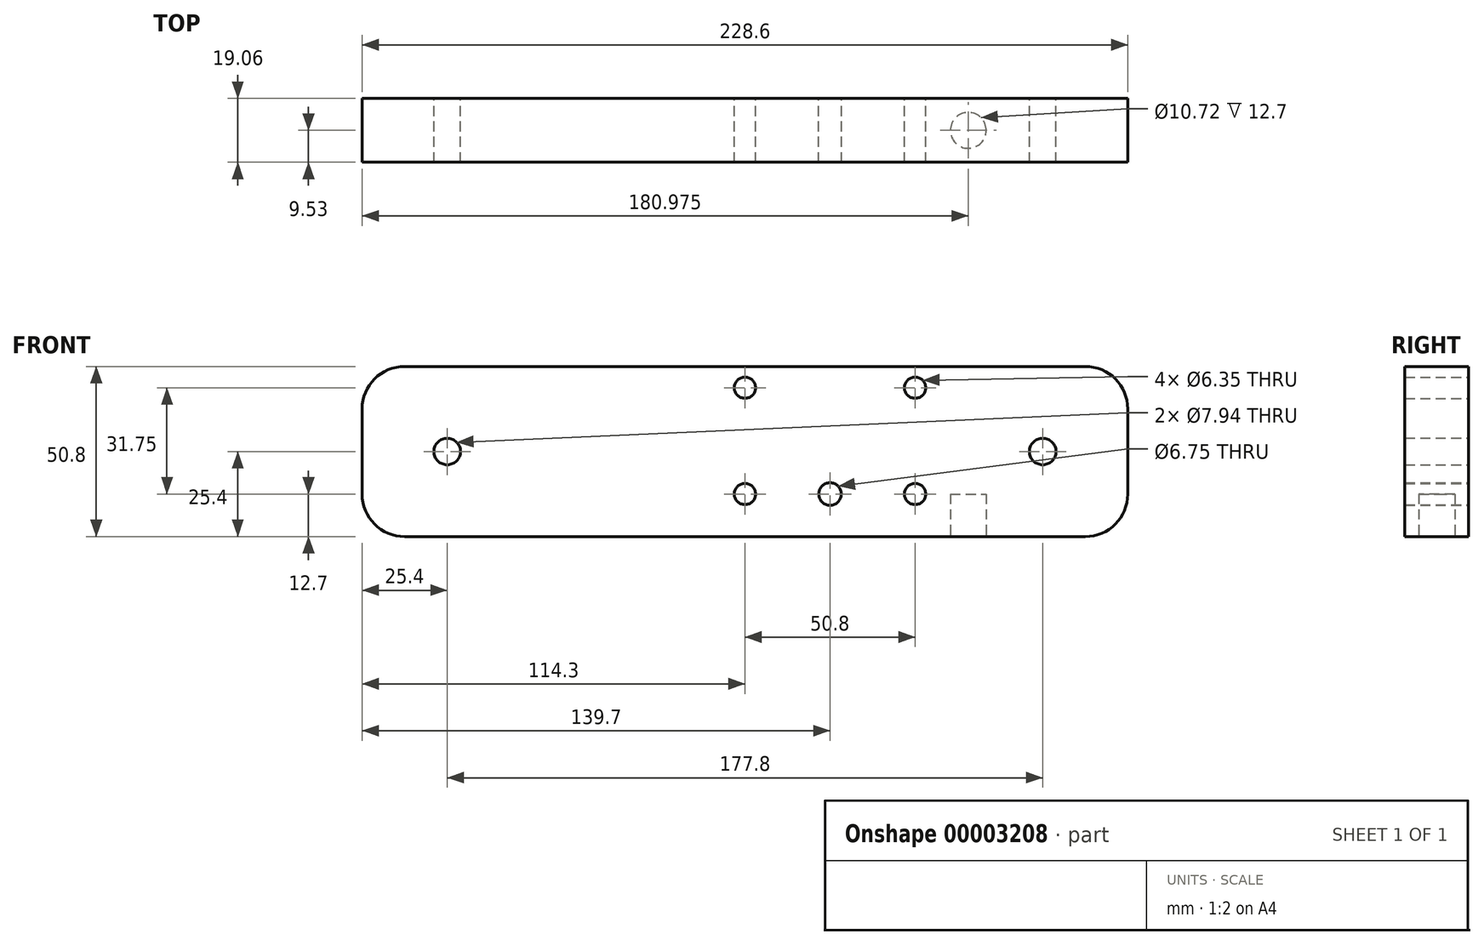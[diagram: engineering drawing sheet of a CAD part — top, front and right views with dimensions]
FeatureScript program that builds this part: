
annotation { "Feature Type Name" : "Feature", "Feature Type Description" : "" }
export const myFeature = defineFeature(function(context is Context, id is Id, definition is map)
    precondition{}
    {
        {
            var Q0;
            Q0=qCreatedBy(makeId("Front.planeOp"),FACE);
            var sketch = newSketch(context, id + "F0", { "sketchPlane" : qUnion([Q0])});
            skLineSegment(sketch, "E0", {"start": v(0, 0) * mm, "end": v(0, -50.8) * mm});
            skLineSegment(sketch, "E1", {"start": v(0, -50.8) * mm, "end": v(228.6, -50.8) * mm});
            skLineSegment(sketch, "E2", {"start": v(228.6, -50.8) * mm, "end": v(228.6, 0) * mm});
            skLineSegment(sketch, "E3", {"start": v(228.6, 0) * mm, "end": v(0, 0) * mm});
            skLineSegment(sketch, "E4", {"start": v(0, -25.4) * mm, "end": v(228.6, -25.4) * mm, "construction": true});
            skLineSegment(sketch, "E5", {"start": v(25.4, 0) * mm, "end": v(25.4, -50.8) * mm, "construction": true});
            skLineSegment(sketch, "E6", {"start": v(203.2, 0) * mm, "end": v(203.2, -50.8) * mm, "construction": true});
            skLineSegment(sketch, "E7", {"start": v(114.3, 0) * mm, "end": v(114.3, -50.8) * mm, "construction": true});
            skLineSegment(sketch, "E8", {"start": v(139.7, 0) * mm, "end": v(139.7, -50.8) * mm, "construction": true});
            skLineSegment(sketch, "E9", {"start": v(0, -6.35) * mm, "end": v(228.6, -6.35) * mm, "construction": true});
            skLineSegment(sketch, "E10", {"start": v(0, -38.1) * mm, "end": v(228.6, -38.1) * mm, "construction": true});
            skLineSegment(sketch, "E11", {"start": v(165.1, 0) * mm, "end": v(165.1, -50.8) * mm, "construction": true});
            skCircle(sketch, "E12", {"center": v(25.4, -25.4) * mm, "radius": 3.97 * mm});
            skCircle(sketch, "E13", {"center": v(114.3, -6.35) * mm, "radius": 3.18 * mm});
            skCircle(sketch, "E14", {"center": v(114.3, -38.1) * mm, "radius": 3.18 * mm});
            skCircle(sketch, "E15", {"center": v(139.7, -38.1) * mm, "radius": 3.37 * mm});
            skCircle(sketch, "E16", {"center": v(165.1, -6.35) * mm, "radius": 3.18 * mm});
            skCircle(sketch, "E17", {"center": v(165.1, -38.1) * mm, "radius": 3.18 * mm});
            skCircle(sketch, "E18", {"center": v(203.2, -25.4) * mm, "radius": 3.97 * mm});
            skSolve(sketch);
        }
        {
            var Q0;
            Q0 = qSketchRegion(id + "F0", true);
            extrude(context, id + "F1", {"entities" : qUnion([Q0]), "endBound" : BoundingType.SYMMETRIC, "depth" : 19.05 * mm});
        }
        {
            var Q0;
            Q0=makeQuery(id+"F1.opExtrude","SWEPT_FACE",FACE,{"disambiguationData":[OSD([sQuery(id+"F0.wireOp",EDGE,"E1")])]});
            var sketch = newSketch(context, id + "F2", { "sketchPlane" : qUnion([Q0])});
            skLineSegment(sketch, "E19", {"start": v(0, 0) * mm, "end": v(228.6, 0) * mm, "construction": true});
            skLineSegment(sketch, "E20", {"start": v(180.98, 9.53) * mm, "end": v(180.98, -9.53) * mm, "construction": true});
            skCircle(sketch, "E21", {"center": v(180.98, 0) * mm, "radius": 5.36 * mm});
            skSolve(sketch);
        }
        {
            var Q0;
            Q0 = qSketchRegion(id + "F2", true);
            extrude(context, id + "F3", {"entities" : qUnion([Q0]), "operationType" : NewBodyOperationType.REMOVE, "oppositeDirection" : true, "depth" : 12.7 * mm});
        }
        {
            var Q0;
            Q0=makeQuery(id+"F1.opExtrude","SWEPT_EDGE",EDGE,{"disambiguationData":[OSD([sQuery(id+"F0.wireOp",EDGE,"E0"),sQuery(id+"F0.wireOp",EDGE,"E3")])]});
            var Q1;
            Q1=makeQuery(id+"F1.opExtrude","SWEPT_EDGE",EDGE,{"disambiguationData":[OSD([sQuery(id+"F0.wireOp",EDGE,"E0"),sQuery(id+"F0.wireOp",EDGE,"E1")])]});
            var Q2;
            Q2=makeQuery(id+"F1.opExtrude","SWEPT_EDGE",EDGE,{"disambiguationData":[OSD([sQuery(id+"F0.wireOp",EDGE,"E2"),sQuery(id+"F0.wireOp",EDGE,"E3")])]});
            var Q3;
            Q3=makeQuery(id+"F1.opExtrude","SWEPT_EDGE",EDGE,{"disambiguationData":[OSD([sQuery(id+"F0.wireOp",EDGE,"E1"),sQuery(id+"F0.wireOp",EDGE,"E2")])]});
            fillet(context, id + "F4", {"entities" : qUnion([Q0, Q1, Q2, Q3]), "radius" : 12.7 * mm, "tangentPropagation" : true, "allowEdgeOverflow" : false});
        }
    });
